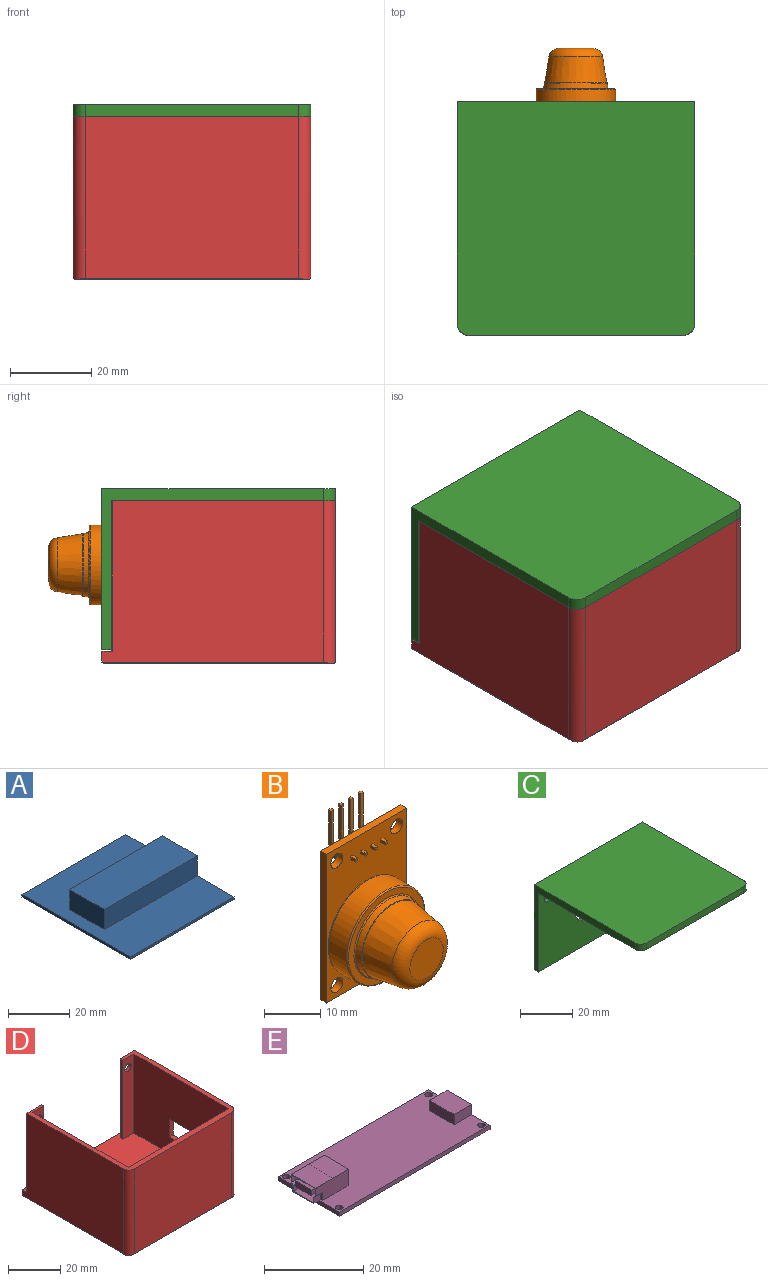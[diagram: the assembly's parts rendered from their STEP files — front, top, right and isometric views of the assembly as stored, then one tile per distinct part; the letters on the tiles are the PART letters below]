
ASSEMBLY  parts=5 mates=4
PART A: 10 faces, bbox 48x50x9 mm
  f0: plane 50x48mm, normal (0,0,1), area 1712mm2, adj f1,f2,f3,f4,f6,f7,f8
  f1: plane 48x1mm, normal (0,-1,0), area 48mm2, adj f0,f2,f4,f5
  f2: plane 50x9mm, normal (1,0,0), area 178mm2, adj f0,f1,f3,f5,f6,f8,f9
  f3: plane 48x1mm, normal (0,1,0), area 48mm2, adj f0,f2,f4,f5
  f4: plane 50x1mm, normal (-1,0,0), area 50mm2, adj f0,f1,f3,f5
  f5: plane 50x48mm, normal (0,0,-1), area 2400mm2, adj f1,f2,f3,f4
  f6: plane 43x8mm, normal (0,1,0), area 344mm2, adj f0,f2,f7,f9
  f7: plane 16x8mm, normal (-1,0,0), area 128mm2, adj f0,f6,f8,f9
  f8: plane 43x8mm, normal (0,-1,0), area 344mm2, adj f0,f2,f7,f9
  f9: plane 43x16mm, normal (0,0,1), area 688mm2, adj f2,f6,f7,f8
PART B: 120 faces, bbox 21.2x20.5x36.3 mm
  f0: plane 32.25x20.1mm, normal (0,1,0), area 595.2mm2, adj f2,f3,f4,f5,f6,f7,f8,f9
  f1: plane 32.25x20.1mm, normal (0,-1,0), area 332mm2, adj f2,f3,f4,f5,f6,f7,f8,f9
  f2: plane 32.25x1.5mm, normal (-1,0,0), area 48.4mm2, adj f0,f1,f3,f5
  f3: plane 20.1x1.5mm, normal (0,0,1), area 30.1mm2, adj f0,f1,f2,f4
  f4: plane 32.25x1.5mm, normal (1,0,0), area 48.4mm2, adj f0,f1,f3,f5
  f5: plane 20.1x1.5mm, normal (0,0,-1), area 30.1mm2, adj f0,f1,f2,f4
  f6: cylinder r=1.5mm len=3mm, axis (0,-1,0), area 14.1mm2, adj f0,f1
  f7: cylinder r=1.5mm len=3mm, axis (0,-1,0), area 14.1mm2, adj f0,f1
  f8: cylinder r=1.5mm len=3mm, axis (0,-1,0), area 14.1mm2, adj f0,f1
  f9: cylinder r=1.5mm len=3mm, axis (0,-1,0), area 14.1mm2, adj f0,f1
  f10: plane 10x2.5mm, normal (0,1,0), area 23.3mm2, adj f11,f12,f13,f14,f15,f16,f17,f18
  f11: cylinder r=0.25mm len=2mm, axis (0,-1,0), area 0.8mm2, adj f0,f10,f12,f36
  f12: cylinder r=0.25mm len=2mm, axis (0,-1,0), area 0.8mm2, adj f0,f10,f11,f13
  f13: plane 2x2mm, normal (0,0,1), area 4mm2, adj f0,f10,f12,f14
  f14: cylinder r=0.25mm len=2mm, axis (0,-1,0), area 0.8mm2, adj f0,f10,f13,f15
  f15: cylinder r=0.25mm len=2mm, axis (0,-1,0), area 0.8mm2, adj f0,f10,f14,f16
  f16: plane 2x2mm, normal (0,0,1), area 4mm2, adj f0,f10,f15,f17
  f17: cylinder r=0.25mm len=2mm, axis (0,-1,0), area 0.8mm2, adj f0,f10,f16,f18
  f18: cylinder r=0.25mm len=2mm, axis (0,-1,0), area 0.8mm2, adj f0,f10,f17,f19
  f19: plane 2x2mm, normal (0,0,1), area 4mm2, adj f0,f10,f18,f20
  f20: cylinder r=0.25mm len=2mm, axis (0,-1,0), area 0.8mm2, adj f0,f10,f19,f21
  f21: plane 2x2mm, normal (1,0,0), area 4mm2, adj f0,f10,f20,f22
  f22: cylinder r=0.25mm len=2mm, axis (0,-1,0), area 0.8mm2, adj f0,f10,f21,f23
  f23: plane 2x2mm, normal (0,0,-1), area 4mm2, adj f0,f10,f22,f24
  f24: cylinder r=0.25mm len=2mm, axis (0,-1,0), area 0.8mm2, adj f0,f10,f23,f25
  f25: cylinder r=0.25mm len=2mm, axis (0,-1,0), area 0.8mm2, adj f0,f10,f24,f26
  f26: plane 2x2mm, normal (0,0,-1), area 4mm2, adj f0,f10,f25,f27
  f27: cylinder r=0.25mm len=2mm, axis (0,-1,0), area 0.8mm2, adj f0,f10,f26,f28
  f28: cylinder r=0.25mm len=2mm, axis (0,-1,0), area 0.8mm2, adj f0,f10,f27,f29
  f29: plane 2x2mm, normal (0,0,-1), area 4mm2, adj f0,f10,f28,f30
  f30: cylinder r=0.25mm len=2mm, axis (0,-1,0), area 0.8mm2, adj f0,f10,f29,f31
  f31: cylinder r=0.25mm len=2mm, axis (0,-1,0), area 0.8mm2, adj f0,f10,f30,f32
  f32: plane 2x2mm, normal (0,0,-1), area 4mm2, adj f0,f10,f31,f33
  f33: cylinder r=0.25mm len=2mm, axis (0,-1,0), area 0.8mm2, adj f0,f10,f32,f34
  f34: plane 2x2mm, normal (-1,0,0), area 4mm2, adj f0,f10,f33,f35
  f35: cylinder r=0.25mm len=2mm, axis (0,-1,0), area 0.8mm2, adj f0,f10,f34,f36
  f36: plane 2x2mm, normal (0,0,1), area 4mm2, adj f0,f10,f11,f35
  f37: plane 0.6x0.6mm, normal (0,0,1), area 0.4mm2, adj f46,f47,f48,f49
  f38: plane 1.1x0.6mm, normal (0,0,-1), area 0.7mm2, adj f10,f39,f41,f43
  f39: plane 1.1x0.6mm, normal (1,0,0), area 0.7mm2, adj f10,f38,f40,f44
  f40: plane 1.1x0.6mm, normal (0,0,1), area 0.7mm2, adj f10,f39,f41,f45
  f41: plane 1.1x0.6mm, normal (-1,0,0), area 0.7mm2, adj f10,f38,f40,f42
  f42: plane 0.9x0.9mm, normal (-1,0,0), area 0.6mm2, adj f41,f43,f45,f46
  f43: cylinder r=0.9mm len=0.9mm, axis (1,0,0), area 0.8mm2, adj f38,f42,f44,f47
  f44: plane 0.9x0.9mm, normal (1,0,0), area 0.6mm2, adj f39,f43,f45,f48
  f45: cylinder r=0.3mm len=0.6mm, axis (1,0,0), area 0.3mm2, adj f40,f42,f44,f49
  f46: plane 7.15x0.6mm, normal (-1,0,0), area 4.3mm2, adj f37,f42,f47,f49
  f47: plane 7.15x0.6mm, normal (0,1,0), area 4.3mm2, adj f37,f43,f46,f48
  f48: plane 7.15x0.6mm, normal (1,0,0), area 4.3mm2, adj f37,f44,f47,f49
  f49: plane 7.15x0.6mm, normal (0,-1,0), area 4.3mm2, adj f37,f45,f46,f48
  f50: plane 1.2x0.6mm, normal (0,0,1), area 0.7mm2, adj f1,f52,f53,f54
  f51: plane 1.2x0.6mm, normal (0,0,-1), area 0.7mm2, adj f1,f52,f53,f54
  f52: plane 1.2x0.6mm, normal (-1,0,0), area 0.7mm2, adj f1,f50,f51,f54
  f53: plane 1.2x0.6mm, normal (1,0,0), area 0.7mm2, adj f1,f50,f51,f54
  f54: plane 0.6x0.6mm, normal (0,-1,0), area 0.4mm2, adj f50,f51,f52,f53
  f55: plane 0.6x0.6mm, normal (0,0,1), area 0.4mm2, adj f64,f65,f66,f67
  f56: plane 1.1x0.6mm, normal (0,0,-1), area 0.7mm2, adj f10,f57,f59,f61
  f57: plane 1.1x0.6mm, normal (1,0,0), area 0.7mm2, adj f10,f56,f58,f62
  f58: plane 1.1x0.6mm, normal (0,0,1), area 0.7mm2, adj f10,f57,f59,f63
  f59: plane 1.1x0.6mm, normal (-1,0,0), area 0.7mm2, adj f10,f56,f58,f60
  f60: plane 0.9x0.9mm, normal (-1,0,0), area 0.6mm2, adj f59,f61,f63,f64
  f61: cylinder r=0.9mm len=0.9mm, axis (1,0,0), area 0.8mm2, adj f56,f60,f62,f65
  f62: plane 0.9x0.9mm, normal (1,0,0), area 0.6mm2, adj f57,f61,f63,f66
  f63: cylinder r=0.3mm len=0.6mm, axis (1,0,0), area 0.3mm2, adj f58,f60,f62,f67
  f64: plane 7.15x0.6mm, normal (-1,0,0), area 4.3mm2, adj f55,f60,f65,f67
  f65: plane 7.15x0.6mm, normal (0,1,0), area 4.3mm2, adj f55,f61,f64,f66
  f66: plane 7.15x0.6mm, normal (1,0,0), area 4.3mm2, adj f55,f62,f65,f67
  f67: plane 7.15x0.6mm, normal (0,-1,0), area 4.3mm2, adj f55,f63,f64,f66
  f68: plane 1.2x0.6mm, normal (-1,0,0), area 0.7mm2, adj f1,f70,f71,f72
  f69: plane 1.2x0.6mm, normal (1,0,0), area 0.7mm2, adj f1,f70,f71,f72
  f70: plane 1.2x0.6mm, normal (0,0,1), area 0.7mm2, adj f1,f68,f69,f72
  f71: plane 1.2x0.6mm, normal (0,0,-1), area 0.7mm2, adj f1,f68,f69,f72
  f72: plane 0.6x0.6mm, normal (0,-1,0), area 0.4mm2, adj f68,f69,f70,f71
  f73: plane 0.6x0.6mm, normal (0,0,1), area 0.4mm2, adj f82,f83,f84,f85
  f74: plane 1.1x0.6mm, normal (0,0,-1), area 0.7mm2, adj f10,f75,f77,f79
  f75: plane 1.1x0.6mm, normal (1,0,0), area 0.7mm2, adj f10,f74,f76,f80
  f76: plane 1.1x0.6mm, normal (0,0,1), area 0.7mm2, adj f10,f75,f77,f81
  f77: plane 1.1x0.6mm, normal (-1,0,0), area 0.7mm2, adj f10,f74,f76,f78
  f78: plane 0.9x0.9mm, normal (-1,0,0), area 0.6mm2, adj f77,f79,f81,f82
  f79: cylinder r=0.9mm len=0.9mm, axis (1,0,0), area 0.8mm2, adj f74,f78,f80,f83
  f80: plane 0.9x0.9mm, normal (1,0,0), area 0.6mm2, adj f75,f79,f81,f84
  f81: cylinder r=0.3mm len=0.6mm, axis (1,0,0), area 0.3mm2, adj f76,f78,f80,f85
  f82: plane 7.15x0.6mm, normal (-1,0,0), area 4.3mm2, adj f73,f78,f83,f85
  f83: plane 7.15x0.6mm, normal (0,1,0), area 4.3mm2, adj f73,f79,f82,f84
  f84: plane 7.15x0.6mm, normal (1,0,0), area 4.3mm2, adj f73,f80,f83,f85
  f85: plane 7.15x0.6mm, normal (0,-1,0), area 4.3mm2, adj f73,f81,f82,f84
  f86: plane 1.2x0.6mm, normal (-1,0,0), area 0.7mm2, adj f1,f88,f89,f90
  f87: plane 1.2x0.6mm, normal (1,0,0), area 0.7mm2, adj f1,f88,f89,f90
  f88: plane 1.2x0.6mm, normal (0,0,1), area 0.7mm2, adj f1,f86,f87,f90
  f89: plane 1.2x0.6mm, normal (0,0,-1), area 0.7mm2, adj f1,f86,f87,f90
  f90: plane 0.6x0.6mm, normal (0,-1,0), area 0.4mm2, adj f86,f87,f88,f89
  f91: plane 0.6x0.6mm, normal (0,0,1), area 0.4mm2, adj f100,f101,f102,f103
  f92: plane 1.1x0.6mm, normal (0,0,-1), area 0.7mm2, adj f10,f93,f95,f97
  f93: plane 1.1x0.6mm, normal (1,0,0), area 0.7mm2, adj f10,f92,f94,f98
  f94: plane 1.1x0.6mm, normal (0,0,1), area 0.7mm2, adj f10,f93,f95,f99
  f95: plane 1.1x0.6mm, normal (-1,0,0), area 0.7mm2, adj f10,f92,f94,f96
  f96: plane 0.9x0.9mm, normal (-1,0,0), area 0.6mm2, adj f95,f97,f99,f100
  f97: cylinder r=0.9mm len=0.9mm, axis (1,0,0), area 0.8mm2, adj f92,f96,f98,f101
  f98: plane 0.9x0.9mm, normal (1,0,0), area 0.6mm2, adj f93,f97,f99,f102
  f99: cylinder r=0.3mm len=0.6mm, axis (1,0,0), area 0.3mm2, adj f94,f96,f98,f103
  f100: plane 7.15x0.6mm, normal (-1,0,0), area 4.3mm2, adj f91,f96,f101,f103
  f101: plane 7.15x0.6mm, normal (0,1,0), area 4.3mm2, adj f91,f97,f100,f102
  f102: plane 7.15x0.6mm, normal (1,0,0), area 4.3mm2, adj f91,f98,f101,f103
  f103: plane 7.15x0.6mm, normal (0,-1,0), area 4.3mm2, adj f91,f99,f100,f102
  f104: plane 1.2x0.6mm, normal (-1,0,0), area 0.7mm2, adj f1,f106,f107,f108
  f105: plane 1.2x0.6mm, normal (1,0,0), area 0.7mm2, adj f1,f106,f107,f108
  f106: plane 1.2x0.6mm, normal (0,0,1), area 0.7mm2, adj f1,f104,f105,f108
  f107: plane 1.2x0.6mm, normal (0,0,-1), area 0.7mm2, adj f1,f104,f105,f108
  f108: plane 0.6x0.6mm, normal (0,-1,0), area 0.4mm2, adj f104,f105,f106,f107
  f109: plane 8.37x8.37mm, normal (0,-1,0), area 55.1mm2, adj f110
  f110: torus R=4.19mm, axis (0,-1,0), area 126.4mm2, adj f109,f111
  f111: cone r=6.66mm half-angle=8.8deg, axis (0,1,0), area 290.4mm2, adj f110,f112
  f112: plane 15.42x15.42mm, normal (0,-1,0), area 2.8mm2, adj f111,f113
  f113: torus R=7.71mm, axis (0,-1,0), area 3.4mm2, adj f112,f114
  f114: cone r=7.76mm half-angle=9.5deg, axis (0,1,0), area 62.6mm2, adj f113,f115
  f115: torus R=8.21mm, axis (0,-1,0), area 17.8mm2, adj f114,f116
  f116: plane 19.1x19.1mm, normal (0,-1,0), area 74.7mm2, adj f115,f117
  f117: torus R=9.55mm, axis (0,-1,0), area 24mm2, adj f116,f118
  f118: cylinder r=9.8mm len=19.6mm, axis (0,-1,0), area 277.1mm2, adj f117,f119
  f119: torus R=9.55mm, axis (0,-1,0), area 24mm2, adj f1,f118
PART C: 13 faces, bbox 58.6x57.6x39.7 mm
  f0: plane 54.6x39.7mm, normal (1,0,0), area 248.2mm2, adj f1,f4,f5,f6,f7,f12
  f1: plane 58.6x39.7mm, normal (0,1,0), area 1960.8mm2, adj f0,f2,f4,f7,f8,f9,f10
  f2: plane 54.6x39.7mm, normal (-1,0,0), area 248.2mm2, adj f1,f4,f5,f6,f7,f11
  f3: plane 52.6x3mm, normal (0,-1,0), area 157.8mm2, adj f4,f5,f11,f12
  f4: plane 58.6x57.6mm, normal (0,0,1), area 3371.5mm2, adj f0,f1,f2,f3,f11,f12
  f5: plane 58.6x55.3mm, normal (0,0,-1), area 3236.7mm2, adj f0,f2,f3,f6,f11,f12
  f6: plane 58.6x36.7mm, normal (0,-1,0), area 1785mm2, adj f0,f2,f5,f7,f8,f9,f10
  f7: plane 58.6x2.3mm, normal (0,0,-1), area 134.8mm2, adj f0,f1,f2,f6
  f8: cylinder r=10.5mm len=21mm, axis (0,1,0), area 151.7mm2, adj f1,f6
  f9: cylinder r=1.75mm len=3.5mm, axis (0,1,0), area 25.3mm2, adj f1,f6
  f10: cylinder r=1.75mm len=3.5mm, axis (0,1,0), area 25.3mm2, adj f1,f6
  f11: cylinder r=3mm len=3mm, axis (0,0,1), area 14.1mm2, adj f2,f3,f4,f5
  f12: cylinder r=3mm len=3mm, axis (0,0,-1), area 14.1mm2, adj f0,f3,f4,f5
PART D: 28 faces, bbox 58.6x57.6x40 mm
  f0: plane 54.6x39.7mm, normal (1,0,0), area 1982.3mm2, adj f2,f4,f7,f15,f16,f17,f18,f19
  f1: plane 51.1x37mm, normal (-1,0,0), area 1791.8mm2, adj f2,f9,f10,f15,f16,f17,f18,f19
  f2: plane 58.6x55.27mm, normal (0,0,1), area 3002.5mm2, adj f0,f1,f4,f5,f7,f8,f9,f10
  f3: plane 52.6x39.7mm, normal (0,-1,0), area 2088.2mm2, adj f15,f23,f26,f27
  f4: plane 58.6x2.7mm, normal (0,1,0), area 158.2mm2, adj f0,f2,f5,f24
  f5: plane 54.6x39.7mm, normal (-1,0,0), area 2069mm2, adj f2,f4,f14,f15,f25,f27
  f6: plane 58x57mm, normal (0,0,-1), area 3304.5mm2, adj f22,f23,f24,f25,f26,f27
  f7: plane 37x8mm, normal (0,1,0), area 286.4mm2, adj f0,f2,f8,f15,f21
  f8: plane 37x1.5mm, normal (-1,0,0), area 55.5mm2, adj f2,f7,f9,f15
  f9: plane 37x6mm, normal (0,-1,0), area 212.4mm2, adj f1,f2,f8,f15,f21
  f10: plane 54.6x37mm, normal (-0.01,1,0), area 2020.2mm2, adj f1,f2,f11,f15
  f11: plane 51.43x37mm, normal (1,0,0), area 1903mm2, adj f2,f10,f12,f15
  f12: plane 37x6mm, normal (0,-1,0), area 212.4mm2, adj f2,f11,f13,f15,f20
  f13: plane 37x1.17mm, normal (1,0,0), area 43.3mm2, adj f2,f12,f14,f15
  f14: plane 37x8mm, normal (0,1,0), area 286.4mm2, adj f2,f5,f13,f15,f20
  f15: plane 58.6x55.27mm, normal (0,0,1), area 369mm2, adj f0,f1,f3,f5,f7,f8,f9,f10
  f16: plane 11.5x2mm, normal (0,0,1), area 23mm2, adj f0,f1,f17,f19
  f17: plane 8.6x2mm, normal (0,-1,0), area 17.2mm2, adj f0,f1,f16,f18
  f18: plane 11.5x2mm, normal (0,0,-1), area 23mm2, adj f0,f1,f17,f19
  f19: plane 8.6x2mm, normal (0,1,0), area 17.2mm2, adj f0,f1,f16,f18
  f20: cylinder r=1.75mm len=3.5mm, axis (0,1,0), area 12.9mm2, adj f12,f14
  f21: cylinder r=1.75mm len=3.5mm, axis (0,1,0), area 16.5mm2, adj f7,f9
  f22: plane 55.91x0.3mm, normal (0.71,0,-0.71), area 23.5mm2, adj f0,f6,f24,f26
  f23: plane 55.22x0.3mm, normal (0,-0.71,-0.71), area 23.1mm2, adj f3,f6,f26,f27
  f24: plane 58.6x0.3mm, normal (0,0.71,-0.71), area 24.7mm2, adj f4,f6,f22,f25
  f25: plane 55.91x0.3mm, normal (-0.71,0,-0.71), area 23.5mm2, adj f5,f6,f24,f27
  f26: cylinder r=3mm len=40mm, axis (0,0,1), area 188mm2, adj f0,f3,f6,f15,f22,f23
  f27: cylinder r=3mm len=40mm, axis (0,0,-1), area 188mm2, adj f3,f5,f6,f15,f23,f25
PART E: 42 faces, bbox 44.5x17.5x5 mm
  f0: plane 6x1.5mm, normal (0,0,-1), area 9mm2, adj f4,f12,f35,f37
  f1: plane 9.5x4mm, normal (0,1,0), area 34mm2, adj f2,f12,f14,f15,f38,f39
  f2: plane 43x17.5mm, normal (0,0,1), area 654.9mm2, adj f1,f3,f4,f5,f6,f7,f8,f9
  f3: plane 43x1mm, normal (0,1,0), area 43mm2, adj f2,f4,f9,f11
  f4: plane 17.5x1mm, normal (-1,0,0), area 17.5mm2, adj f0,f2,f3,f5,f11
  f5: plane 43x1mm, normal (0,-1,0), area 43mm2, adj f2,f4,f9,f11
  f6: cylinder r=0.75mm len=1.5mm, axis (0,0,1), area 4.7mm2, adj f2,f11
  f7: cylinder r=0.75mm len=1.5mm, axis (0,0,1), area 4.7mm2, adj f2,f11
  f8: cylinder r=0.75mm len=1.5mm, axis (0,0,1), area 4.7mm2, adj f2,f11
  f9: plane 17.5x3.5mm, normal (1,0,0), area 35mm2, adj f2,f3,f5,f11,f16,f18,f19
  f10: cylinder r=0.75mm len=1.5mm, axis (0,0,1), area 4.7mm2, adj f2,f11
  f11: plane 43x17.5mm, normal (0,0,-1), area 745.4mm2, adj f3,f4,f5,f6,f7,f8,f9,f10
  f12: plane 7x4mm, normal (-1,0,0), area 2.1mm2, adj f0,f1,f13,f15,f20,f21,f22,f23
  f13: plane 9.5x4mm, normal (0,-1,0), area 34mm2, adj f2,f12,f14,f15,f34,f36
  f14: plane 7x4mm, normal (1,0,0), area 28mm2, adj f1,f2,f13,f15
  f15: plane 9.5x7mm, normal (0,0,1), area 66.5mm2, adj f1,f12,f13,f14
  f16: plane 5x2.5mm, normal (0,1,0), area 12.5mm2, adj f2,f9,f17,f19
  f17: plane 7x2.5mm, normal (-1,0,0), area 17.5mm2, adj f2,f16,f18,f19
  f18: plane 5x2.5mm, normal (0,-1,0), area 12.5mm2, adj f2,f9,f17,f19
  f19: plane 7x5mm, normal (0,0,1), area 35mm2, adj f9,f16,f17,f18
  f20: plane 5.8x5mm, normal (0,0,1), area 29mm2, adj f12,f21,f31,f32
  f21: plane 5x1.44mm, normal (0,1,0), area 7.2mm2, adj f12,f20,f22,f32
  f22: plane 5x0.5mm, normal (0,0.71,0.71), area 3.5mm2, adj f12,f21,f23,f32
  f23: plane 5x1.86mm, normal (0,1,0), area 9.3mm2, adj f12,f22,f24,f32
  f24: plane 6.8x5mm, normal (0,0,-1), area 34mm2, adj f12,f23,f25,f32
  f25: plane 5x1.86mm, normal (0,-1,0), area 9.3mm2, adj f12,f24,f26,f32
  f26: plane 5x0.5mm, normal (0,-0.71,0.71), area 3.5mm2, adj f12,f25,f31,f32
  f27: plane 5x3.98mm, normal (0,0,-1), area 19.9mm2, adj f32,f33,f40,f41
  f28: plane 5x1.1mm, normal (0,1,0), area 5.5mm2, adj f29,f32,f33,f40
  f29: plane 5x4.78mm, normal (0,0,1), area 23.9mm2, adj f28,f30,f32,f33
  f30: plane 5x1.1mm, normal (0,-1,0), area 5.5mm2, adj f29,f32,f33,f41
  f31: plane 5x1.44mm, normal (0,-1,0), area 7.2mm2, adj f12,f20,f26,f32
  f32: plane 6.8x3.8mm, normal (-1,0,0), area 17.1mm2, adj f20,f21,f22,f23,f24,f25,f26,f27
  f33: plane 4.78x1.5mm, normal (-1,0,0), area 7mm2, adj f27,f28,f29,f30,f40,f41
  f34: plane 2x0.5mm, normal (0,-0.71,-0.71), area 1.4mm2, adj f12,f13,f35,f36
  f35: plane 2x1.5mm, normal (0,-1,0), area 3mm2, adj f0,f2,f12,f34,f36
  f36: plane 2x0.5mm, normal (-1,0,0), area 0.9mm2, adj f2,f13,f34,f35
  f37: plane 2x1.5mm, normal (0,1,0), area 3mm2, adj f0,f2,f12,f38,f39
  f38: plane 2x0.5mm, normal (0,0.71,-0.71), area 1.4mm2, adj f1,f12,f37,f39
  f39: plane 2x0.5mm, normal (-1,0,0), area 0.9mm2, adj f1,f2,f37,f38
  f40: plane 5x0.4mm, normal (0,0.71,-0.71), area 2.8mm2, adj f27,f28,f32,f33
  f41: plane 5x0.4mm, normal (0,-0.71,-0.71), area 2.8mm2, adj f27,f30,f32,f33
PLACE A t=(-62.34,-5.47,-16.97)mm
PLACE B rot(axis=(1,0,0),180deg) t=(-72.39,20.28,16.28)mm
PLACE C t=(-62.29,-6.68,20.03)mm
PLACE D t=(-61.29,-6.68,-19.97)mm
PLACE E rot(axis=(0,0,1),180deg) t=(-59.84,-5.47,-6.97)mm
MATE parallel E.f11 <-> A.f9  axis (0,0,-1) through (-38.34,-5.47,-7.97)mm
MATE parallel C.f5 <-> D.f15  axis (0,0,-1) through (-62.29,-35.48,20.03)mm
MATE parallel B.f3 <-> A.f0  axis (0,0,-1) through (-62.34,19.53,-15.97)mm
MATE parallel D.f2 <-> A.f5  axis (0,0,1) through (-62.34,-5.47,-16.97)mm
